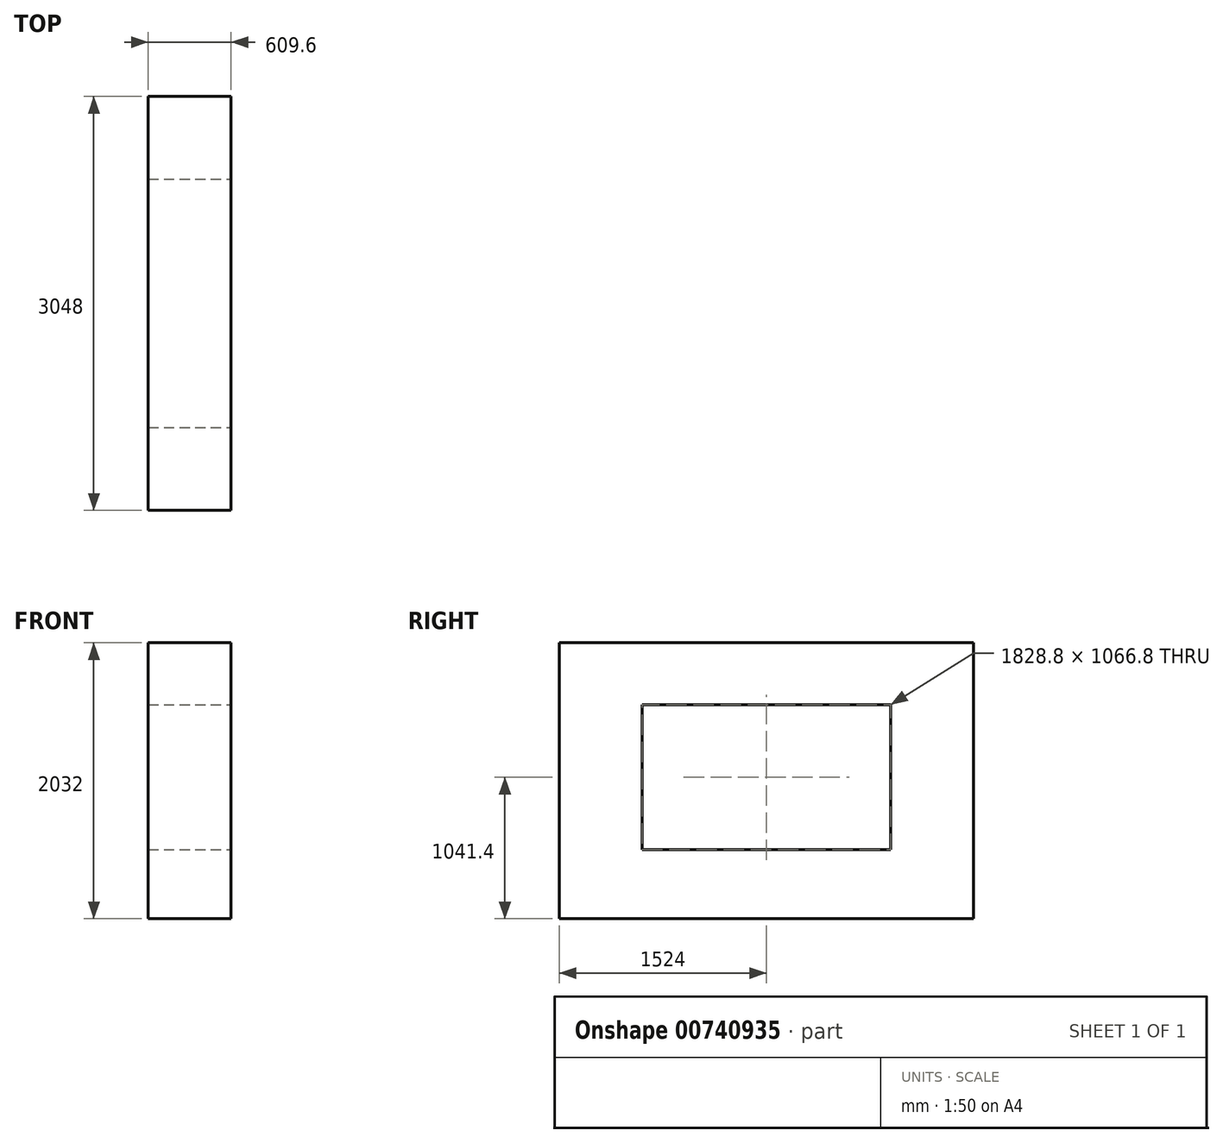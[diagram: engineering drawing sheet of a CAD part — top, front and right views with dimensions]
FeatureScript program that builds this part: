
annotation { "Feature Type Name" : "Feature", "Feature Type Description" : "" }
export const myFeature = defineFeature(function(context is Context, id is Id, definition is map)
    precondition{}
    {
        {
            var Q0;
            Q0=qCreatedBy(makeId("Top.planeOp"),FACE);
            var sketch = newSketch(context, id + "F0", { "sketchPlane" : qUnion([Q0])});
            skLineSegment(sketch, "E0.bottom", {"start": v(0, -317.85) * mm, "end": v(609.6, -317.85) * mm});
            skLineSegment(sketch, "E0.top", {"start": v(0, 1510.95) * mm, "end": v(609.6, 1510.95) * mm});
            skLineSegment(sketch, "E0.left", {"start": v(0, -317.85) * mm, "end": v(0, 1510.95) * mm});
            skLineSegment(sketch, "E0.right", {"start": v(609.6, -317.85) * mm, "end": v(609.6, 1510.95) * mm});
            skLineSegment(sketch, "E1.top", {"start": v(0, -927.45) * mm, "end": v(609.6, -927.45) * mm});
            skLineSegment(sketch, "E1.left", {"start": v(0, -317.85) * mm, "end": v(0, -927.45) * mm});
            skLineSegment(sketch, "E1.right", {"start": v(609.6, -317.85) * mm, "end": v(609.6, -927.45) * mm});
            skLineSegment(sketch, "E2.top", {"start": v(0, 2120.55) * mm, "end": v(609.6, 2120.55) * mm});
            skLineSegment(sketch, "E2.left", {"start": v(0, 1510.95) * mm, "end": v(0, 2120.55) * mm});
            skLineSegment(sketch, "E2.right", {"start": v(609.6, 1510.95) * mm, "end": v(609.6, 2120.55) * mm});
            skSolve(sketch);
        }
        {
            var Q0;
            Q0=makeQuery(id+"F0.imprint","IMPRINT",FACE,{"disambiguationData":[TD([[makeQuery(id+"F0.imprint","IMPRINT",EDGE,{"derivedFrom":sQuery(id+"F0.wireOp",EDGE,"E0.left")}),-1.0]])]});
            extrude(context, id + "F1", {"entities" : qUnion([Q0]), "depth" : 508 * mm, "offsetDistance" : 25.4 * mm});
        }
        {
            var Q0;
            Q0=qCreatedBy(makeId("Top.planeOp"),FACE);
            var sketch = newSketch(context, id + "F2", { "sketchPlane" : qUnion([Q0])});
            skLineSegment(sketch, "E3.bottom", {"start": v(31.75, 1479.2) * mm, "end": v(82.55, 1479.2) * mm});
            skLineSegment(sketch, "E3.top", {"start": v(31.75, 1428.4) * mm, "end": v(82.55, 1428.4) * mm});
            skLineSegment(sketch, "E3.left", {"start": v(31.75, 1479.2) * mm, "end": v(31.75, 1428.4) * mm});
            skLineSegment(sketch, "E3.right", {"start": v(82.55, 1479.2) * mm, "end": v(82.55, 1428.4) * mm});
            skLineSegment(sketch, "E4.bottom", {"start": v(514.35, 1479.2) * mm, "end": v(565.15, 1479.2) * mm});
            skLineSegment(sketch, "E4.top", {"start": v(514.35, 1428.4) * mm, "end": v(565.15, 1428.4) * mm});
            skLineSegment(sketch, "E4.left", {"start": v(514.35, 1479.2) * mm, "end": v(514.35, 1428.4) * mm});
            skLineSegment(sketch, "E4.right", {"start": v(565.15, 1479.2) * mm, "end": v(565.15, 1428.4) * mm});
            skLineSegment(sketch, "E5.bottom", {"start": v(0, 1510.95) * mm, "end": v(596.9, 1510.95) * mm});
            skLineSegment(sketch, "E5.top", {"start": v(0, 1479.2) * mm, "end": v(596.9, 1479.2) * mm});
            skLineSegment(sketch, "E5.left", {"start": v(0, 1510.95) * mm, "end": v(0, 1479.2) * mm});
            skLineSegment(sketch, "E5.right", {"start": v(596.9, 1510.95) * mm, "end": v(596.9, 1479.2) * mm});
            skLineSegment(sketch, "E6.bottom", {"start": v(0, 1479.2) * mm, "end": v(31.75, 1479.2) * mm});
            skLineSegment(sketch, "E6.top", {"start": v(0, -273.4) * mm, "end": v(31.75, -273.4) * mm});
            skLineSegment(sketch, "E6.left", {"start": v(0, 1479.2) * mm, "end": v(0, -273.4) * mm});
            skLineSegment(sketch, "E6.right", {"start": v(31.75, 1479.2) * mm, "end": v(31.75, -273.4) * mm});
            skLineSegment(sketch, "E7.bottom", {"start": v(0, -305.15) * mm, "end": v(596.9, -305.15) * mm});
            skLineSegment(sketch, "E7.top", {"start": v(0, -273.4) * mm, "end": v(596.9, -273.4) * mm});
            skLineSegment(sketch, "E7.left", {"start": v(0, -305.15) * mm, "end": v(0, -273.4) * mm});
            skLineSegment(sketch, "E7.right", {"start": v(596.9, -305.15) * mm, "end": v(596.9, -273.4) * mm});
            skLineSegment(sketch, "E8.bottom", {"start": v(596.9, -273.4) * mm, "end": v(565.15, -273.4) * mm});
            skLineSegment(sketch, "E8.top", {"start": v(596.9, 1479.2) * mm, "end": v(565.15, 1479.2) * mm});
            skLineSegment(sketch, "E8.left", {"start": v(596.9, -273.4) * mm, "end": v(596.9, 1479.2) * mm});
            skLineSegment(sketch, "E8.right", {"start": v(565.15, -273.4) * mm, "end": v(565.15, 1479.2) * mm});
            skLineSegment(sketch, "E9.bottom", {"start": v(31.75, 946.86) * mm, "end": v(565.15, 946.86) * mm});
            skLineSegment(sketch, "E9.top", {"start": v(31.75, 915.11) * mm, "end": v(565.15, 915.11) * mm});
            skLineSegment(sketch, "E9.left", {"start": v(31.75, 946.86) * mm, "end": v(31.75, 915.11) * mm});
            skLineSegment(sketch, "E9.right", {"start": v(565.15, 946.86) * mm, "end": v(565.15, 915.11) * mm});
            skLineSegment(sketch, "E10.bottom", {"start": v(31.75, 290.7) * mm, "end": v(565.15, 290.7) * mm});
            skLineSegment(sketch, "E10.top", {"start": v(31.75, 258.95) * mm, "end": v(565.15, 258.95) * mm});
            skLineSegment(sketch, "E10.left", {"start": v(31.75, 290.7) * mm, "end": v(31.75, 258.95) * mm});
            skLineSegment(sketch, "E10.right", {"start": v(565.15, 290.7) * mm, "end": v(565.15, 258.95) * mm});
            skLineSegment(sketch, "E11.bottom", {"start": v(31.75, 915.11) * mm, "end": v(82.55, 915.11) * mm});
            skLineSegment(sketch, "E11.top", {"start": v(31.75, 864.31) * mm, "end": v(82.55, 864.31) * mm});
            skLineSegment(sketch, "E11.left", {"start": v(31.75, 915.11) * mm, "end": v(31.75, 864.31) * mm});
            skLineSegment(sketch, "E11.right", {"start": v(82.55, 915.11) * mm, "end": v(82.55, 864.31) * mm});
            skLineSegment(sketch, "E12.bottom", {"start": v(514.35, 915.11) * mm, "end": v(565.15, 915.11) * mm});
            skLineSegment(sketch, "E12.top", {"start": v(514.35, 864.31) * mm, "end": v(565.15, 864.31) * mm});
            skLineSegment(sketch, "E12.left", {"start": v(514.35, 915.11) * mm, "end": v(514.35, 864.31) * mm});
            skLineSegment(sketch, "E12.right", {"start": v(565.15, 915.11) * mm, "end": v(565.15, 864.31) * mm});
            skLineSegment(sketch, "E13.bottom", {"start": v(31.75, 341.5) * mm, "end": v(82.55, 341.5) * mm});
            skLineSegment(sketch, "E13.top", {"start": v(31.75, 290.7) * mm, "end": v(82.55, 290.7) * mm});
            skLineSegment(sketch, "E13.left", {"start": v(31.75, 341.5) * mm, "end": v(31.75, 290.7) * mm});
            skLineSegment(sketch, "E13.right", {"start": v(82.55, 341.5) * mm, "end": v(82.55, 290.7) * mm});
            skLineSegment(sketch, "E14.bottom", {"start": v(514.35, 341.5) * mm, "end": v(565.15, 341.5) * mm});
            skLineSegment(sketch, "E14.top", {"start": v(514.35, 290.7) * mm, "end": v(565.15, 290.7) * mm});
            skLineSegment(sketch, "E14.left", {"start": v(514.35, 341.5) * mm, "end": v(514.35, 290.7) * mm});
            skLineSegment(sketch, "E14.right", {"start": v(565.15, 341.5) * mm, "end": v(565.15, 290.7) * mm});
            skLineSegment(sketch, "E15", {"start": v(902.88, 1510.95) * mm, "end": v(902.88, 905.59) * mm, "construction": true});
            skLineSegment(sketch, "E16", {"start": v(902.88, 905.59) * mm, "end": v(902.88, 300.22) * mm, "construction": true});
            skLineSegment(sketch, "E17", {"start": v(902.88, 300.22) * mm, "end": v(902.88, -305.15) * mm, "construction": true});
            skLineSegment(sketch, "E18", {"start": v(565.15, 341.5) * mm, "end": v(565.15, 258.95) * mm, "construction": true});
            skPoint(sketch, "E19", {"position": v(565.15, 300.22) * mm});
            skLineSegment(sketch, "E20", {"start": v(565.15, 946.86) * mm, "end": v(565.15, 864.31) * mm, "construction": true});
            skPoint(sketch, "E21", {"position": v(565.15, 905.59) * mm});
            skLineSegment(sketch, "E22.bottom", {"start": v(31.75, -222.6) * mm, "end": v(82.55, -222.6) * mm});
            skLineSegment(sketch, "E22.top", {"start": v(31.75, -273.4) * mm, "end": v(82.55, -273.4) * mm});
            skLineSegment(sketch, "E22.left", {"start": v(31.75, -222.6) * mm, "end": v(31.75, -273.4) * mm});
            skLineSegment(sketch, "E22.right", {"start": v(82.55, -222.6) * mm, "end": v(82.55, -273.4) * mm});
            skLineSegment(sketch, "E23.bottom", {"start": v(514.35, -222.6) * mm, "end": v(565.15, -222.6) * mm});
            skLineSegment(sketch, "E23.top", {"start": v(514.35, -273.4) * mm, "end": v(565.15, -273.4) * mm});
            skLineSegment(sketch, "E23.left", {"start": v(514.35, -222.6) * mm, "end": v(514.35, -273.4) * mm});
            skLineSegment(sketch, "E23.right", {"start": v(565.15, -222.6) * mm, "end": v(565.15, -273.4) * mm});
            skLineSegment(sketch, "E24.bottom", {"start": v(609.6, -317.85) * mm, "end": v(596.9, -317.85) * mm});
            skLineSegment(sketch, "E24.top", {"start": v(609.6, 1510.95) * mm, "end": v(596.9, 1510.95) * mm});
            skLineSegment(sketch, "E24.left", {"start": v(609.6, -317.85) * mm, "end": v(609.6, 1510.95) * mm});
            skLineSegment(sketch, "E24.right", {"start": v(596.9, -317.85) * mm, "end": v(596.9, 1510.95) * mm});
            skLineSegment(sketch, "E25.top", {"start": v(0, -317.85) * mm, "end": v(596.9, -317.85) * mm});
            skLineSegment(sketch, "E25.left", {"start": v(0, -305.15) * mm, "end": v(0, -317.85) * mm});
            skLineSegment(sketch, "E25.right", {"start": v(596.9, -305.15) * mm, "end": v(596.9, -317.85) * mm});
            skSolve(sketch);
        }
        {
            var Q0;
            Q0=qCreatedBy(makeId("Top.planeOp"),FACE);
            var sketch = newSketch(context, id + "F3", { "sketchPlane" : qUnion([Q0])});
            skLineSegment(sketch, "E26.bottom", {"start": v(31.75, 2076.1) * mm, "end": v(82.55, 2076.1) * mm});
            skLineSegment(sketch, "E26.top", {"start": v(31.75, 2025.3) * mm, "end": v(82.55, 2025.3) * mm});
            skLineSegment(sketch, "E26.left", {"start": v(31.75, 2076.1) * mm, "end": v(31.75, 2025.3) * mm});
            skLineSegment(sketch, "E26.right", {"start": v(82.55, 2076.1) * mm, "end": v(82.55, 2025.3) * mm});
            skLineSegment(sketch, "E27.bottom", {"start": v(514.35, 2076.1) * mm, "end": v(565.15, 2076.1) * mm});
            skLineSegment(sketch, "E27.top", {"start": v(514.35, 2025.3) * mm, "end": v(565.15, 2025.3) * mm});
            skLineSegment(sketch, "E27.left", {"start": v(514.35, 2076.1) * mm, "end": v(514.35, 2025.3) * mm});
            skLineSegment(sketch, "E27.right", {"start": v(565.15, 2076.1) * mm, "end": v(565.15, 2025.3) * mm});
            skLineSegment(sketch, "E28.bottom", {"start": v(514.35, 1593.5) * mm, "end": v(565.15, 1593.5) * mm});
            skLineSegment(sketch, "E28.top", {"start": v(514.35, 1542.7) * mm, "end": v(565.15, 1542.7) * mm});
            skLineSegment(sketch, "E28.left", {"start": v(514.35, 1593.5) * mm, "end": v(514.35, 1542.7) * mm});
            skLineSegment(sketch, "E28.right", {"start": v(565.15, 1593.5) * mm, "end": v(565.15, 1542.7) * mm});
            skLineSegment(sketch, "E29.bottom", {"start": v(31.75, 1593.5) * mm, "end": v(82.55, 1593.5) * mm});
            skLineSegment(sketch, "E29.top", {"start": v(31.75, 1542.7) * mm, "end": v(82.55, 1542.7) * mm});
            skLineSegment(sketch, "E29.left", {"start": v(31.75, 1593.5) * mm, "end": v(31.75, 1542.7) * mm});
            skLineSegment(sketch, "E29.right", {"start": v(82.55, 1593.5) * mm, "end": v(82.55, 1542.7) * mm});
            skLineSegment(sketch, "E30.bottom", {"start": v(31.75, 2107.85) * mm, "end": v(565.15, 2107.85) * mm});
            skLineSegment(sketch, "E30.top", {"start": v(31.75, 2076.1) * mm, "end": v(565.15, 2076.1) * mm});
            skLineSegment(sketch, "E30.left", {"start": v(31.75, 2107.85) * mm, "end": v(31.75, 2076.1) * mm});
            skLineSegment(sketch, "E30.right", {"start": v(565.15, 2107.85) * mm, "end": v(565.15, 2076.1) * mm});
            skLineSegment(sketch, "E31.top", {"start": v(596.9, 1510.95) * mm, "end": v(549.76, 1510.95) * mm});
            skLineSegment(sketch, "E32.bottom", {"start": v(565.15, 1510.95) * mm, "end": v(31.75, 1510.95) * mm});
            skLineSegment(sketch, "E32.top", {"start": v(565.15, 1542.7) * mm, "end": v(31.75, 1542.7) * mm});
            skLineSegment(sketch, "E32.left", {"start": v(565.15, 1510.95) * mm, "end": v(565.15, 1542.7) * mm});
            skLineSegment(sketch, "E32.right", {"start": v(31.75, 1510.95) * mm, "end": v(31.75, 1542.7) * mm});
            skLineSegment(sketch, "E33.bottom", {"start": v(0, 2107.85) * mm, "end": v(31.75, 2107.85) * mm});
            skLineSegment(sketch, "E33.top", {"start": v(0, 1510.95) * mm, "end": v(31.75, 1510.95) * mm});
            skLineSegment(sketch, "E33.left", {"start": v(0, 2107.85) * mm, "end": v(0, 1510.95) * mm});
            skLineSegment(sketch, "E33.right", {"start": v(31.75, 2107.85) * mm, "end": v(31.75, 1510.95) * mm});
            skLineSegment(sketch, "E34.bottom", {"start": v(596.9, 2107.85) * mm, "end": v(565.15, 2107.85) * mm});
            skLineSegment(sketch, "E34.top", {"start": v(596.9, 1510.95) * mm, "end": v(565.15, 1510.95) * mm});
            skLineSegment(sketch, "E34.left", {"start": v(596.9, 2107.85) * mm, "end": v(596.9, 1510.95) * mm});
            skLineSegment(sketch, "E34.right", {"start": v(565.15, 2107.85) * mm, "end": v(565.15, 1510.95) * mm});
            skLineSegment(sketch, "E35.bottom", {"start": v(609.6, 2120.55) * mm, "end": v(596.9, 2120.55) * mm});
            skLineSegment(sketch, "E35.top", {"start": v(609.6, 1510.95) * mm, "end": v(596.9, 1510.95) * mm});
            skLineSegment(sketch, "E35.left", {"start": v(609.6, 2120.55) * mm, "end": v(609.6, 1510.95) * mm});
            skLineSegment(sketch, "E35.right", {"start": v(596.9, 2120.55) * mm, "end": v(596.9, 1510.95) * mm});
            skLineSegment(sketch, "E36.bottom", {"start": v(596.9, 2120.55) * mm, "end": v(0, 2120.55) * mm});
            skLineSegment(sketch, "E36.top", {"start": v(596.9, 2107.85) * mm, "end": v(0, 2107.85) * mm});
            skLineSegment(sketch, "E36.left", {"start": v(596.9, 2120.55) * mm, "end": v(596.9, 2107.85) * mm});
            skLineSegment(sketch, "E36.right", {"start": v(0, 2120.55) * mm, "end": v(0, 2107.85) * mm});
            skLineSegment(sketch, "E37.bottom", {"start": v(0, 2120.55) * mm, "end": v(596.9, 2120.55) * mm});
            skLineSegment(sketch, "E37.top", {"start": v(0, 2107.85) * mm, "end": v(596.9, 2107.85) * mm});
            skSolve(sketch);
        }
        {
            var Q0;
            Q0=qCreatedBy(makeId("Top.planeOp"),FACE);
            var sketch = newSketch(context, id + "F4", { "sketchPlane" : qUnion([Q0])});
            skLineSegment(sketch, "E38.bottom", {"start": v(0, 2120.55) * mm, "end": v(609.6, 2120.55) * mm});
            skLineSegment(sketch, "E38.top", {"start": v(0, -927.45) * mm, "end": v(609.6, -927.45) * mm});
            skLineSegment(sketch, "E38.left", {"start": v(0, 2120.55) * mm, "end": v(0, -927.45) * mm});
            skLineSegment(sketch, "E38.right", {"start": v(609.6, 2120.55) * mm, "end": v(609.6, -927.45) * mm});
            skSolve(sketch);
        }
        {
            var Q0;
            Q0=makeQuery(id+"F4.imprint","IMPRINT",FACE,{"disambiguationData":[TD([[makeQuery(id+"F4.imprint","IMPRINT",EDGE,{"derivedFrom":sQuery(id+"F4.wireOp",EDGE,"E38.bottom")}),-1.0]])]});
            extrude(context, id + "F5", {"entities" : qUnion([Q0]), "operationType" : NewBodyOperationType.ADD, "depth" : 2032 * mm, "offsetDistance" : 25.4 * mm});
        }
        {
            var Q0;
            Q0=makeQuery(id+"F5.boolean.opBoolean","MERGE",FACE,{"derivedFrom":[makeQuery(id+"F1.opExtrude","SWEPT_FACE",FACE,{"disambiguationData":[OSD([sQuery(id+"F0.wireOp",EDGE,"E0.right")])]}),makeQuery(id+"F5.opExtrude","SWEPT_FACE",FACE,{"disambiguationData":[OSD([sQuery(id+"F4.wireOp",EDGE,"E38.right")])]})]});
            var sketch = newSketch(context, id + "F6", { "sketchPlane" : qUnion([Q0])});
            skLineSegment(sketch, "E39.bottom", {"start": v(-317.85, 1574.8) * mm, "end": v(1510.95, 1574.8) * mm});
            skLineSegment(sketch, "E39.top", {"start": v(-317.85, 508) * mm, "end": v(1510.95, 508) * mm});
            skLineSegment(sketch, "E39.left", {"start": v(-317.85, 1574.8) * mm, "end": v(-317.85, 508) * mm});
            skLineSegment(sketch, "E39.right", {"start": v(1510.95, 1574.8) * mm, "end": v(1510.95, 508) * mm});
            skLineSegment(sketch, "E40", {"start": v(-927.45, 1308.53) * mm, "end": v(-317.85, 1308.53) * mm, "construction": true});
            skLineSegment(sketch, "E41", {"start": v(1510.95, 1102.9) * mm, "end": v(2120.55, 1102.9) * mm, "construction": true});
            skSolve(sketch);
        }
        {
            var Q0;
            Q0=makeQuery(id+"F6.imprint","IMPRINT",FACE,{"disambiguationData":[TD([[makeQuery(id+"F6.imprint","IMPRINT",EDGE,{"derivedFrom":sQuery(id+"F6.wireOp",EDGE,"E39.bottom")}),-1.0]])]});
            extrude(context, id + "F7", {"entities" : qUnion([Q0]), "operationType" : NewBodyOperationType.REMOVE, "endBound" : BoundingType.UP_TO_NEXT, "oppositeDirection" : true, "depth" : 25.4 * mm, "offsetDistance" : 25.4 * mm});
        }
    });
